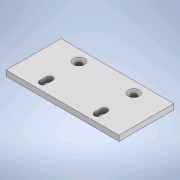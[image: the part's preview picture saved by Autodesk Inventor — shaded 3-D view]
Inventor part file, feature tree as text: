
AUTODESK INVENTOR PART (.ipt)
format: ipt  version: 2020.1 (Build 241239000, 239)  size: 143,360 bytes
history: native  units: mm
features: sketch x3, extrude x2, hole x1
ambient origin geometry x8: Origin, YZ Plane, XZ Plane, XY Plane, X Axis, Y Axis, Z Axis, Center Point
bodies: Volumenkörper1 (feature_tree)
feature tree (6):
  extrude  "Extrusion1"  Depth=100.0mm
  extrude  "Extrusion2"  Depth=10.0mm
  hole  "Bohrung1"  [1 undecoded]
  sketch  "Skizze1"  dims[d0=206.0mm d1=100.0mm]
  sketch  "Skizze2"  dims[d2=10.0mm d3=0.0mm d4=80.0mm]
  sketch  "Skizze4"  dims[d5=90.0deg d6=206.0mm d7=90.0deg d8=103.0mm d9=180.0deg d10=50.0mm d11=0.0mm d12=6.0mm d13=6.0mm d14=6.0mm d15=6.0mm d16=80.0mm d17=90.0deg d18=10.0mm d19=0.0mm d24=20.0mm d25=90.0deg d26=206.0mm d27=90.0deg d28=50.0mm d29=100.0mm d30=0.0mm d31=11.0mm d32=6.0mm d33=20.0mm d34=2.0mm d35=90.0deg d36=8.0mm d37=20.594885mm d38=0.75mm d39=20.594885mm d40=0.0625mm d41=0.75mm d42=0.375mm]
note: 1 required parameter value undecoded (feature->parameter linkage not recoverable at this tier; creation-order binding heuristic only, values carry confidence <= 0.55)
